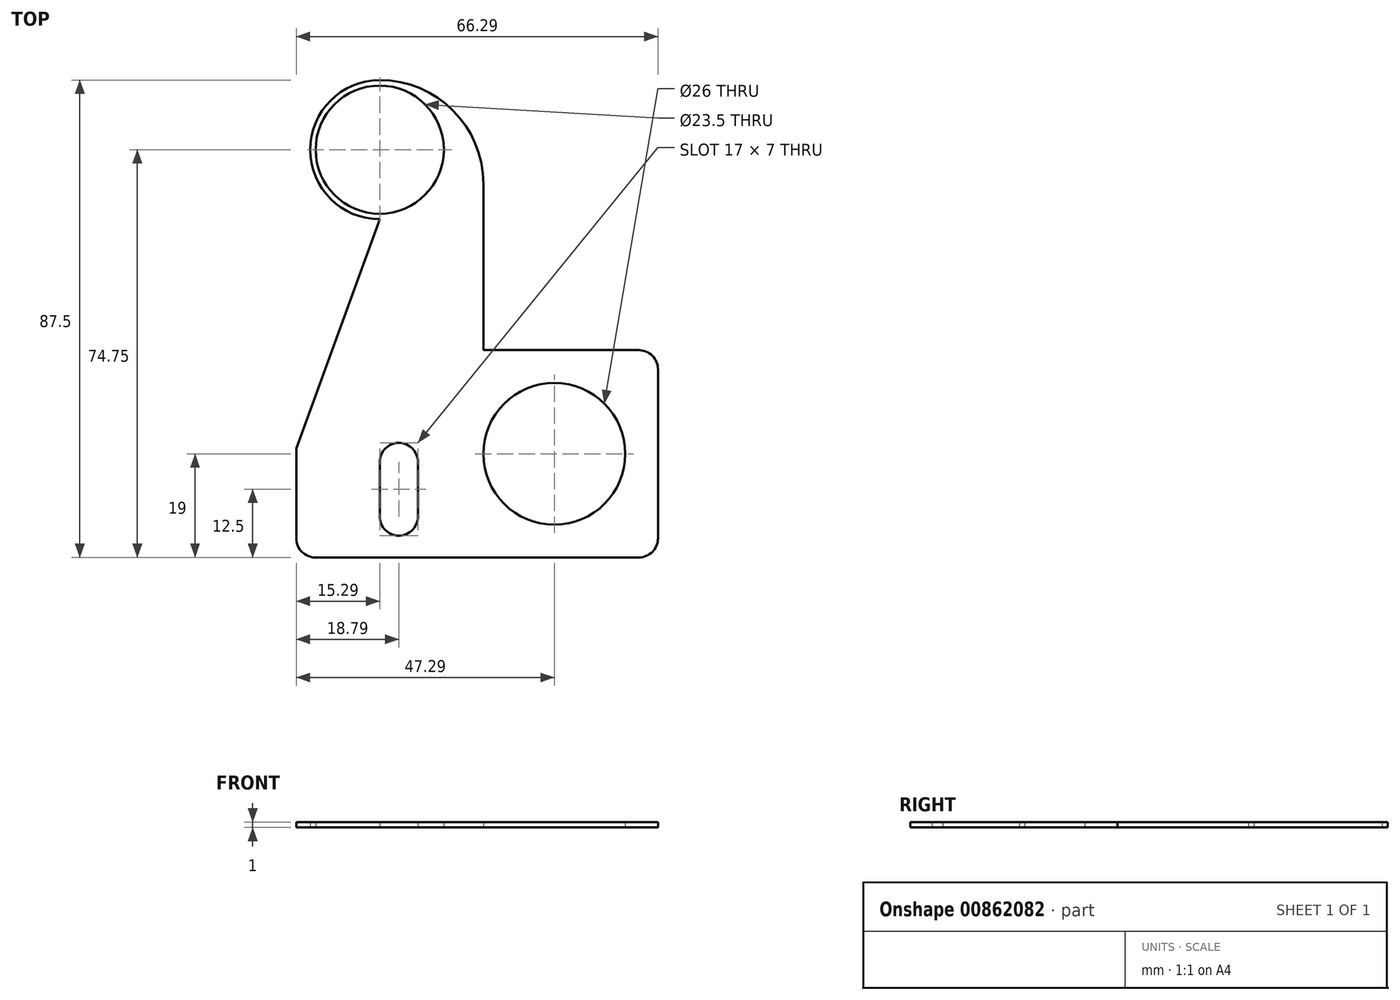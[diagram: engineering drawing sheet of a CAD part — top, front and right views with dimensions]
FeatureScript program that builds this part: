
annotation { "Feature Type Name" : "Feature", "Feature Type Description" : "" }
export const myFeature = defineFeature(function(context is Context, id is Id, definition is map)
    precondition{}
    {
        {
            var Q0;
            Q0=qCreatedBy(makeId("Top.planeOp"),FACE);
            var sketch = newSketch(context, id + "F0", { "sketchPlane" : qUnion([Q0])});
            skLineSegment(sketch, "E0.bottom", {"start": v(-3.5, 0) * mm, "end": v(-3.5, 0) * mm});
            skLineSegment(sketch, "E0.top", {"start": v(-3.5, -17) * mm, "end": v(-3.5, -17) * mm});
            skLineSegment(sketch, "E0.left", {"start": v(0, -3.5) * mm, "end": v(0, -13.5) * mm});
            skLineSegment(sketch, "E0.right", {"start": v(-7, -3.5) * mm, "end": v(-7, -13.5) * mm});
            skLineSegment(sketch, "E1", {"start": v(-7, -8.5) * mm, "end": v(12, -8.5) * mm, "construction": true});
            skCircle(sketch, "E2", {"center": v(25, -2) * mm, "radius": 13 * mm});
            skPoint(sketch, "E2.first.point", {"position": v(12, -2) * mm});
            skPoint(sketch, "E2.second.point", {"position": v(37.9, -3.6) * mm});
            skPoint(sketch, "E2.third.point", {"position": v(37.68, 0.87) * mm});
            skLineSegment(sketch, "E3", {"start": v(25, -2) * mm, "end": v(44, -2) * mm, "construction": true});
            skLineSegment(sketch, "E4", {"start": v(25, -2) * mm, "end": v(25, -21) * mm, "construction": true});
            skLineSegment(sketch, "E5", {"start": v(0, 42) * mm, "end": v(-44.98, 42) * mm, "construction": true});
            skCircle(sketch, "E6", {"center": v(-7, 53.75) * mm, "radius": 11.75 * mm});
            skCircle(sketch, "E7", {"center": v(-7, 53.75) * mm, "radius": 12.75 * mm});
            skLineSegment(sketch, "E8", {"start": v(52.2, 0) * mm, "end": v(52.2, 44) * mm, "construction": true});
            skLineSegment(sketch, "E9", {"start": v(52.2, 44) * mm, "end": v(4.14, 44) * mm, "construction": true});
            skLineSegment(sketch, "E10", {"start": v(-7, 41) * mm, "end": v(-22.29, -1) * mm});
            skLineSegment(sketch, "E11", {"start": v(-14.22, 42) * mm, "end": v(-14.22, -1) * mm, "construction": true});
            skLineSegment(sketch, "E12", {"start": v(-14.22, -1) * mm, "end": v(-39.76, -1) * mm, "construction": true});
            skLineSegment(sketch, "E13", {"start": v(-7, -17) * mm, "end": v(-7, -21) * mm, "construction": true});
            skLineSegment(sketch, "E14", {"start": v(-7, -21) * mm, "end": v(-18.79, -21) * mm, "construction": true});
            skLineSegment(sketch, "E15", {"start": v(44, -2) * mm, "end": v(44, -17.5) * mm, "construction": true});
            skLineSegment(sketch, "E16", {"start": v(25, 17) * mm, "end": v(40.5, 17) * mm, "construction": true});
            skPoint(sketch, "E17", {"position": v(-7, 66.5) * mm});
            skArc(sketch, "E18", {"start": v(12, 47.5) * mm, "mid": v(6.44, 60.94) * mm, "end": v(-7, 66.5) * mm});
            skLineSegment(sketch, "E19", {"start": v(-22.29, -1) * mm, "end": v(-22.29, -17.5) * mm});
            skLineSegment(sketch, "E20", {"start": v(-18.79, -21) * mm, "end": v(40.5, -21) * mm});
            skLineSegment(sketch, "E21", {"start": v(44, -17.5) * mm, "end": v(44, 13.5) * mm});
            skLineSegment(sketch, "E22", {"start": v(40.5, 17) * mm, "end": v(12, 17) * mm});
            skLineSegment(sketch, "E23", {"start": v(12, 17) * mm, "end": v(12, 47.5) * mm});
            skPoint(sketch, "E24.visualSharp", {"position": v(-7, 0) * mm});
            skArc(sketch, "E24.filletArc", {"start": v(-3.5, 0) * mm, "mid": v(-5.97, -1.03) * mm, "end": v(-7, -3.5) * mm});
            skPoint(sketch, "E25.visualSharp", {"position": v(0, 0) * mm});
            skArc(sketch, "E25.filletArc", {"start": v(0, -3.5) * mm, "mid": v(-1.03, -1.03) * mm, "end": v(-3.5, 0) * mm});
            skPoint(sketch, "E26.visualSharp", {"position": v(0, -17) * mm});
            skArc(sketch, "E26.filletArc", {"start": v(-3.5, -17) * mm, "mid": v(-1.03, -15.97) * mm, "end": v(0, -13.5) * mm});
            skPoint(sketch, "E27.visualSharp", {"position": v(-7, -17) * mm});
            skArc(sketch, "E27.filletArc", {"start": v(-7, -13.5) * mm, "mid": v(-5.97, -15.97) * mm, "end": v(-3.5, -17) * mm});
            skArc(sketch, "E28.filletArc", {"start": v(-22.29, -17.5) * mm, "mid": v(-21.26, -19.97) * mm, "end": v(-18.79, -21) * mm});
            skArc(sketch, "E29.filletArc", {"start": v(40.5, -21) * mm, "mid": v(42.97, -19.97) * mm, "end": v(44, -17.5) * mm});
            skArc(sketch, "E30.filletArc", {"start": v(44, 13.5) * mm, "mid": v(42.97, 15.97) * mm, "end": v(40.5, 17) * mm});
            skSolve(sketch);
        }
        {
            var Q0;
            Q0=makeQuery(id+"F0.imprint","IMPRINT",FACE,{"disambiguationData":[TD([[makeQuery(id+"F0.imprint","IMPRINT",EDGE,{"derivedFrom":sQuery(id+"F0.wireOp",EDGE,"E0.left")}),1.0]])]});
            var Q1;
            Q1=makeQuery(id+"F0.imprint","IMPRINT",FACE,{"disambiguationData":[TD([[makeQuery(id+"F0.imprint","IMPRINT",EDGE,{"derivedFrom":sQuery(id+"F0.wireOp",EDGE,"E6")}),-1.0]])]});
            extrude(context, id + "F1", {"entities" : qUnion([Q0, Q1]), "depth" : 1 * mm, "offsetDistance" : 25 * mm});
        }
    });
